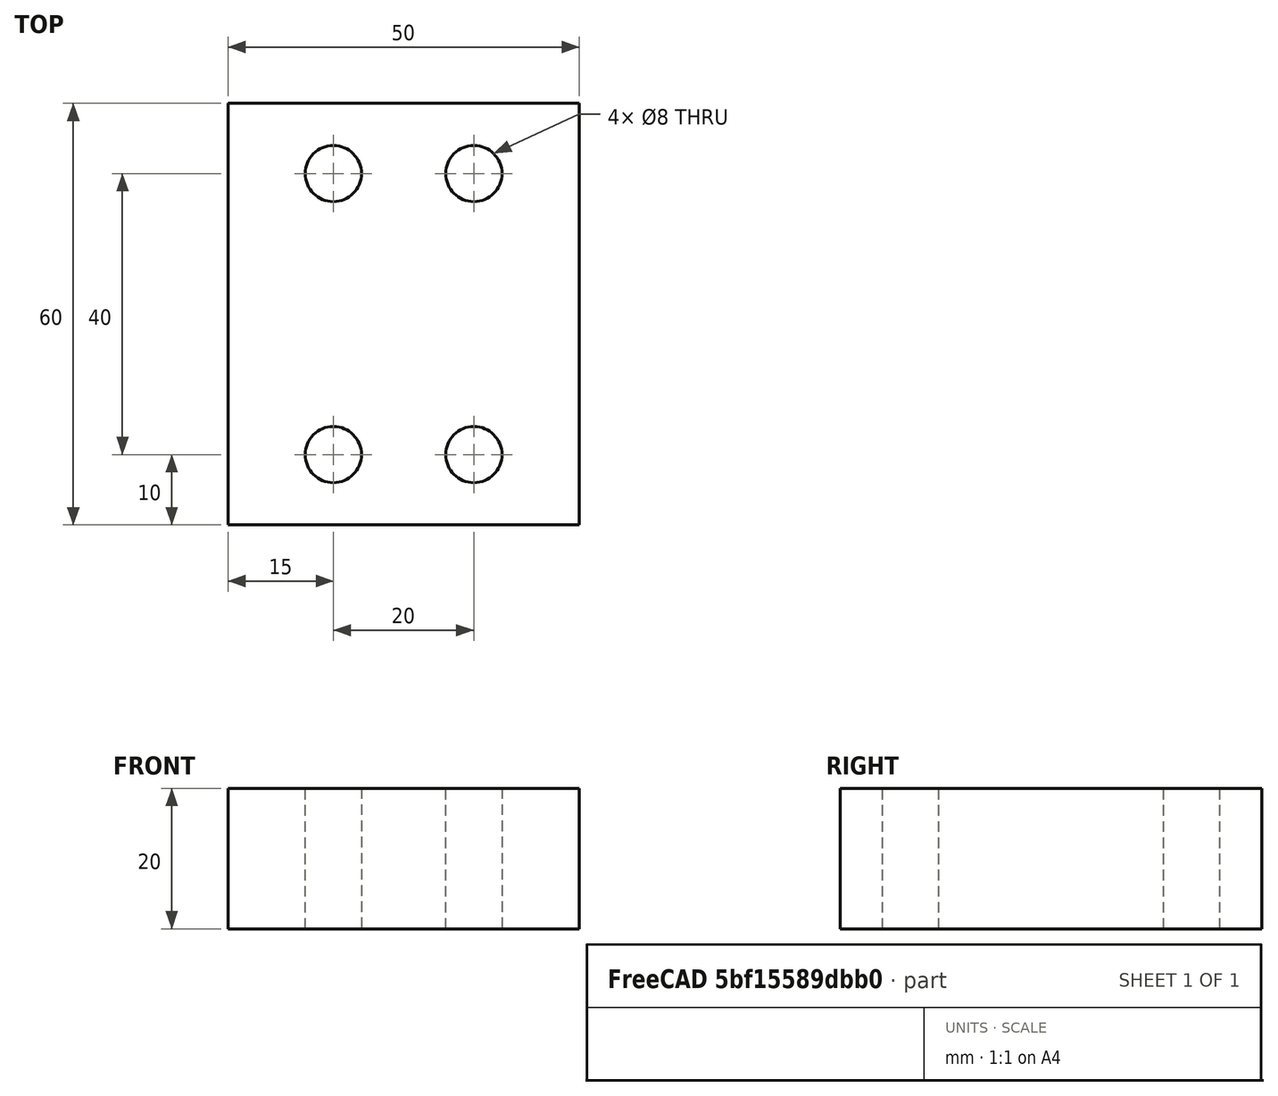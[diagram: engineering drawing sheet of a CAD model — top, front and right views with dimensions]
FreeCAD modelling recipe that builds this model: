
FCSTD DOCUMENT  (FreeCAD 0.19R17089 +1543 (Git))
Label: import-link-001
License: All rights reserved
LicenseURL: http://en.wikipedia.org/wiki/All_rights_reserved
objects: App::FeaturePython×40, Part::FeaturePython×40, App::Link×10, App::LinkElement×8, Sketcher::SketchObject×1, PartDesign::Pad×1, PartDesign::Body×1, App::DocumentObjectGroup×1
note: 40 computed .brp shape members not serialized (recipe doc carries the construction recipe); baked Part::Feature solids carry a one-line shape summary decoded from their .brp
EXTERNAL_REF file=xrepo-lib-003.FCStd obj=Assembly
EXTERNAL_REF file=xrepo-lib-003.FCStd obj=Assembly001
EXTERNAL_REF file=xrepo-lib-003.FCStd obj=Assembly002

FEATURE [Sketcher::SketchObject] Sketch006
  MapMode = 5
  Support = -> [XY_Plane003]
  sketch-geometry (8):
    g0: Circle CenterX=-10 CenterY=20 CenterZ=0 NormalX=0 NormalY=0 NormalZ=1 AngleXU=0 Radius=4
    g1: Circle CenterX=10 CenterY=20 CenterZ=0 NormalX=0 NormalY=0 NormalZ=1 AngleXU=0 Radius=4
    g2: Circle CenterX=10 CenterY=-20 CenterZ=0 NormalX=0 NormalY=0 NormalZ=1 AngleXU=0 Radius=4
    g3: Circle CenterX=-10 CenterY=-20 CenterZ=0 NormalX=0 NormalY=0 NormalZ=1 AngleXU=0 Radius=4
    g4: LineSegment StartX=-25 StartY=30 StartZ=0 EndX=25 EndY=30 EndZ=0
    g5: LineSegment StartX=25 StartY=30 StartZ=0 EndX=25 EndY=-30 EndZ=0
    g6: LineSegment StartX=25 StartY=-30 StartZ=0 EndX=-25 EndY=-30 EndZ=0
    g7: LineSegment StartX=-25 StartY=-30 StartZ=0 EndX=-25 EndY=30 EndZ=0
  constraints (19):
    c: Equal(g0,g1)
    c: Equal(g1,g2)
    c: Equal(g2,g3)
    c: Diameter(g0) = 8  'BHD'
    c: Symmetric(g0,g1,g-2)
    c: Symmetric(g1,g2,g-1)
    c: Symmetric(g0,g3,g-1)
    c: Coincident(g4,g5)
    c: Coincident(g5,g6)
    c: Coincident(g6,g7)
    c: Coincident(g7,g4)
    c: Horizontal(g6)
    c: Vertical(g7)
    c: Symmetric(g4,g4,g-2)
    c: Symmetric(g4,g5,g-1)
    c: Distance(g3,g2) = 20  'L1'
    c: Distance(g4) = 50  'L2'
    c: Distance(g1,g2) = 40  'W1'
    c: Distance(g7) = 60  'W2'
FEATURE [PartDesign::Pad] Pad005
  ClaimChildren = false
  Length = 20
  Length2 = 100
  Profile = -> Sketch006
  Reversed = true
  Type = 0
FEATURE [PartDesign::Body] Body003
  Group = -> [Sketch006,Pad005]
  Origin = -> Origin003
  Tip = -> Pad005
FEATURE [App::FeaturePython] Constraints003  # WARN: FeaturePython — macro-defined, semantics opaque (R4)
  GroupMode = 1
  _Version = 1
FEATURE [Part::FeaturePython] Parts003  # WARN: FeaturePython — macro-defined, semantics opaque (R4)
  Group = -> [Body003]
  GroupMode = 0
FEATURE [App::Link] Link  label="Assembly000 001"
  LinkPlacement = pos=(0,0,-2) rot=(0,0,1;0rad)
  LinkedObject = -> Link007
  Placement = pos=(0,0,-2) rot=(0,0,1;0rad)
FEATURE [App::Link] Link001  label="Assembly001 001"
  LinkedObject = -> Link008
FEATURE [Part::FeaturePython] Parts004  # WARN: FeaturePython — macro-defined, semantics opaque (R4)
  Group = -> [Link,Link001]
  GroupMode = 0
FEATURE [App::Link] Link002  label="Assembly000 002"
  LinkedObject = -> Link007
FEATURE [App::Link] Link003  label="Assembly002 001"
  LinkPlacement = pos=(0,0,2) rot=(0,0,1;0rad)
  LinkedObject = -> Link009
  Placement = pos=(0,0,2) rot=(0,0,1;0rad)
FEATURE [Part::FeaturePython] Parts005  # WARN: FeaturePython — macro-defined, semantics opaque (R4)
  Group = -> [Link002,Link003]
  GroupMode = 0
FEATURE [App::Link] Link004  label="Assembly003 001"
  LinkedObject = -> Assembly003
FEATURE [App::LinkElement] Link005_i0
  LinkPlacement = pos=(-10,20,0) rot=(0,0,1;0rad)
  LinkedObject = -> Assembly005
  Placement = pos=(-10,20,0) rot=(0,0,1;0rad)
FEATURE [App::LinkElement] Link005_i1
  LinkPlacement = pos=(10,20,0) rot=(0,0,1;0rad)
  LinkedObject = -> Assembly005
  Placement = pos=(10,20,0) rot=(0,0,1;0rad)
FEATURE [App::LinkElement] Link005_i2
  LinkPlacement = pos=(10,-20,0) rot=(0,0,1;0rad)
  LinkedObject = -> Assembly005
  Placement = pos=(10,-20,0) rot=(0,0,1;0rad)
FEATURE [App::LinkElement] Link005_i3
  LinkPlacement = pos=(-10,-20,0) rot=(0,0,1;0rad)
  LinkedObject = -> Assembly005
  Placement = pos=(-10,-20,0) rot=(0,0,1;0rad)
FEATURE [App::Link] Link005  label="Assembly005 001"
  ElementCount = 4
  ElementList = -> [Link005_i0,Link005_i1,Link005_i2,Link005_i3]
  LinkedObject = -> Assembly005
FEATURE [App::LinkElement] Link006_i0
  LinkPlacement = pos=(10,20,-33) rot=(0,-1,0;0rad)
  LinkedObject = -> Assembly004
  Placement = pos=(10,20,-33) rot=(0,-1,0;0rad)
FEATURE [App::LinkElement] Link006_i1
  LinkPlacement = pos=(-10,20,-33) rot=(0,-1,0;0rad)
  LinkedObject = -> Assembly004
  Placement = pos=(-10,20,-33) rot=(0,-1,0;0rad)
FEATURE [App::LinkElement] Link006_i2
  LinkPlacement = pos=(-10,-20,-33) rot=(0,-1,0;0rad)
  LinkedObject = -> Assembly004
  Placement = pos=(-10,-20,-33) rot=(0,-1,0;0rad)
FEATURE [App::LinkElement] Link006_i3
  LinkPlacement = pos=(10,-20,-33) rot=(0,-1,0;0rad)
  LinkedObject = -> Assembly004
  Placement = pos=(10,-20,-33) rot=(0,-1,0;0rad)
FEATURE [App::Link] Link006  label="Assembly004 001"
  ElementCount = 4
  ElementList = -> [Link006_i0,Link006_i1,Link006_i2,Link006_i3]
  LinkPlacement = pos=(8.1e-13,6.55651e-06,-55) rot=(0,1,0;3.14159rad)
  LinkedObject = -> Assembly004
  Placement = pos=(8.1e-13,6.55651e-06,-55) rot=(0,1,0;3.14159rad)
FEATURE [Part::FeaturePython] Parts006  # WARN: FeaturePython — macro-defined, semantics opaque (R4)
  Group = -> [Link004,Link005,Link006]
  GroupMode = 0
FEATURE [App::Link] Link007  label="Assembly000 003"
  LinkedObject = -> <external xrepo-lib-003.FCStd>#Assembly
FEATURE [App::Link] Link008  label="Assembly001 002"
  LinkedObject = -> <external xrepo-lib-003.FCStd>#Assembly001
FEATURE [App::Link] Link009  label="Assembly002 002"
  LinkedObject = -> <external xrepo-lib-003.FCStd>#Assembly002
FEATURE [App::DocumentObjectGroup] Group  label="Repository"
  Group = -> [Link007,Link008,Link009,Assembly003,Assembly004,Assembly005]
FEATURE [Part::FeaturePython] Assembly003  label="Assembly003 000"  # WARN: FeaturePython — macro-defined, semantics opaque (R4)
  AutoRelax = true
  BuildShape = 0
  Freeze = false
  Group = -> [Constraints003,Elements003,Parts003]
  GroupMode = 1
  SolverType = 1
  Verbose = false
  _SolverType = 1
  _Version = 1
FEATURE [App::FeaturePython] Elements003  # WARN: FeaturePython — macro-defined, semantics opaque (R4)
  Group = -> [Element005,Element006,Element007,Element008,Element009,Element010,Element011,Element012,Element015]
  GroupMode = 1
FEATURE [Part::FeaturePython] Element005  # link proxy (typed FeaturePython)
  Detach = false
  LinkTransform = true
  LinkedObject = -> Body003 [Pad005.Edge23]
  _Parent = -> Elements003
FEATURE [Part::FeaturePython] Element006  # link proxy (typed FeaturePython)
  Detach = false
  LinkTransform = true
  LinkedObject = -> Body003 [Pad005.Edge20]
  _Parent = -> Elements003
FEATURE [Part::FeaturePython] Element007  # link proxy (typed FeaturePython)
  Detach = false
  LinkTransform = true
  LinkedObject = -> Body003 [Pad005.Edge17]
  _Parent = -> Elements003
FEATURE [Part::FeaturePython] Element008  # link proxy (typed FeaturePython)
  Detach = false
  LinkTransform = true
  LinkedObject = -> Body003 [Pad005.Edge14]
  _Parent = -> Elements003
FEATURE [Part::FeaturePython] Element009  # link proxy (typed FeaturePython)
  Detach = false
  LinkTransform = true
  LinkedObject = -> Body003 [Pad005.Edge24]
  _Parent = -> Elements003
FEATURE [Part::FeaturePython] Element010  # link proxy (typed FeaturePython)
  Detach = false
  LinkTransform = true
  LinkedObject = -> Body003 [Pad005.Edge21]
  _Parent = -> Elements003
FEATURE [Part::FeaturePython] Element011  # link proxy (typed FeaturePython)
  Detach = false
  LinkTransform = true
  LinkedObject = -> Body003 [Pad005.Edge18]
  _Parent = -> Elements003
FEATURE [Part::FeaturePython] Element012  # link proxy (typed FeaturePython)
  Detach = false
  LinkTransform = true
  LinkedObject = -> Body003 [Pad005.Edge15]
  _Parent = -> Elements003
FEATURE [Part::FeaturePython] Assembly004  label="Assembly004 000"  # WARN: FeaturePython — macro-defined, semantics opaque (R4)
  AutoRelax = true
  BuildShape = 0
  Freeze = false
  Group = -> [Constraints004,Elements004,Parts004]
  GroupMode = 1
  SolverType = 1
  Verbose = false
  _SolverType = 1
  _Version = 1
FEATURE [App::FeaturePython] Constraints004  # WARN: FeaturePython — macro-defined, semantics opaque (R4)
  Group = -> [Constraint]
  GroupMode = 1
  _Version = 1
FEATURE [App::FeaturePython] Elements004  # WARN: FeaturePython — macro-defined, semantics opaque (R4)
  Group = -> [_Element,_Element001,Element013]
  GroupMode = 1
FEATURE [App::FeaturePython] Constraint  label="PlaneCoincident"  # WARN: FeaturePython — macro-defined, semantics opaque (R4)
  Angle = 0
  AnglePitch = 0
  AngleRoll = 0
  Cascade = false
  ConstraintType = 2
  Disabled = false
  Group = -> [ElementLink,ElementLink001]
  GroupMode = 1
  LockAngle = false
  Multiply = false
  OffsetX = 0
  OffsetY = 0
  _ConstraintType = 35
  _Parent = -> Constraints004
FEATURE [App::FeaturePython] ElementLink  label="_Element"  # link proxy (typed FeaturePython)
  LinkTransform = true
  LinkedObject = -> _Element
  _Parent = -> Constraint
FEATURE [Part::FeaturePython] _Element  # link proxy (typed FeaturePython)
  Detach = false
  LinkTransform = true
  LinkedObject = -> Link001 [1.$Element002.]
  _Parent = -> Elements004
FEATURE [App::FeaturePython] ElementLink001  label="_Element001"  # link proxy (typed FeaturePython)
  LinkTransform = true
  LinkedObject = -> _Element001
  _Parent = -> Constraint
FEATURE [Part::FeaturePython] _Element001  # link proxy (typed FeaturePython)
  Detach = false
  LinkTransform = true
  LinkedObject = -> Link [1.$Element001.]
  _Parent = -> Elements004
FEATURE [Part::FeaturePython] Element013  # link proxy (typed FeaturePython)
  Detach = false
  LinkTransform = true
  LinkedObject = -> Link [1.$Element.]
  _Parent = -> Elements004
FEATURE [Part::FeaturePython] Assembly005  label="Assembly005 000"  # WARN: FeaturePython — macro-defined, semantics opaque (R4)
  AutoRelax = true
  BuildShape = 0
  Freeze = false
  Group = -> [Constraints005,Elements005,Parts005]
  GroupMode = 1
  SolverType = 1
  Verbose = false
  _SolverType = 1
  _Version = 1
FEATURE [App::FeaturePython] Constraints005  # WARN: FeaturePython — macro-defined, semantics opaque (R4)
  Group = -> [Constraint001]
  GroupMode = 1
  _Version = 1
FEATURE [App::FeaturePython] Elements005  # WARN: FeaturePython — macro-defined, semantics opaque (R4)
  Group = -> [_Element002,_Element003,Element014]
  GroupMode = 1
FEATURE [App::FeaturePython] Constraint001  label="PlaneCoincident001"  # WARN: FeaturePython — macro-defined, semantics opaque (R4)
  Angle = 0
  AnglePitch = 0
  AngleRoll = 0
  Cascade = false
  ConstraintType = 2
  Disabled = false
  Group = -> [ElementLink002,ElementLink003]
  GroupMode = 1
  LockAngle = false
  Multiply = false
  OffsetX = 0
  OffsetY = 0
  _ConstraintType = 35
  _Parent = -> Constraints005
FEATURE [App::FeaturePython] ElementLink002  label="_Element002"  # link proxy (typed FeaturePython)
  LinkTransform = true
  LinkedObject = -> _Element002
  _Parent = -> Constraint001
FEATURE [Part::FeaturePython] _Element002  # link proxy (typed FeaturePython)
  Detach = false
  LinkTransform = true
  LinkedObject = -> Link002 [1.$Element001.]
  _Parent = -> Elements005
FEATURE [App::FeaturePython] ElementLink003  label="_Element003"  # link proxy (typed FeaturePython)
  LinkTransform = true
  LinkedObject = -> _Element003
  _Parent = -> Constraint001
FEATURE [Part::FeaturePython] _Element003  # link proxy (typed FeaturePython)
  Detach = false
  LinkTransform = true
  LinkedObject = -> Link003 [1.$Element004.]
  _Parent = -> Elements005
FEATURE [Part::FeaturePython] Element014  # link proxy (typed FeaturePython)
  Detach = false
  LinkTransform = true
  LinkedObject = -> Link002 [1.$Element.]
  _Parent = -> Elements005
FEATURE [Part::FeaturePython] Assembly006  label="Assembly006 000"  # WARN: FeaturePython — macro-defined, semantics opaque (R4)
  AutoRelax = true
  BuildShape = 0
  Freeze = false
  Group = -> [Constraints006,Elements006,Parts006]
  GroupMode = 1
  SolverType = 1
  Verbose = false
  _SolverType = 1
  _Version = 1
FEATURE [App::FeaturePython] Constraints006  # WARN: FeaturePython — macro-defined, semantics opaque (R4)
  Group = -> [Constraint002,Constraint003,Constraint004,Constraint005,Constraint006,Constraint007,Constraint008,Constraint009,Constraint010]
  GroupMode = 1
  _Version = 1
FEATURE [App::FeaturePython] Elements006  # WARN: FeaturePython — macro-defined, semantics opaque (R4)
  Group = -> [_Element004,_Element005,_Element006,_Element007,_Element008,_Element009,_Element010,_Element011,_Element012,_Element013,_Element014,_Element015,_Element016,_Element017,_Element018,_Element019,_Element020]
  GroupMode = 1
FEATURE [App::FeaturePython] Constraint002  label="Locked"  # WARN: FeaturePython — macro-defined, semantics opaque (R4)
  ConstraintType = 0
  Disabled = false
  Group = -> [ElementLink004]
  GroupMode = 1
  _ConstraintType = 0
  _Parent = -> Constraints006
FEATURE [App::FeaturePython] ElementLink004  label="_Element004"  # link proxy (typed FeaturePython)
  LinkTransform = true
  LinkedObject = -> _Element004
  _Parent = -> Constraint002
FEATURE [Part::FeaturePython] Element015  # link proxy (typed FeaturePython)
  Detach = false
  LinkTransform = true
  LinkedObject = -> Body003 [Pad005.Face9]
  _Parent = -> Elements003
FEATURE [Part::FeaturePython] _Element004  # link proxy (typed FeaturePython)
  Detach = false
  LinkTransform = true
  LinkedObject = -> Link004 [1.$Element015.]
  _Parent = -> Elements006
FEATURE [App::FeaturePython] Constraint003  label="PlaneCoincident002"  # WARN: FeaturePython — macro-defined, semantics opaque (R4)
  Angle = 0
  AnglePitch = 0
  AngleRoll = 0
  Cascade = false
  ConstraintType = 2
  Disabled = false
  Group = -> [ElementLink005,ElementLink006]
  GroupMode = 1
  LockAngle = false
  Multiply = false
  OffsetX = 0
  OffsetY = 0
  _ConstraintType = 35
  _Parent = -> Constraints006
FEATURE [App::FeaturePython] ElementLink005  label="_Element005"  # link proxy (typed FeaturePython)
  LinkTransform = true
  LinkedObject = -> _Element005
  _Parent = -> Constraint003
FEATURE [Part::FeaturePython] _Element005  # link proxy (typed FeaturePython)
  Detach = false
  LinkTransform = true
  LinkedObject = -> Link005 [Link005_i0.1.$Element014.]
  _Parent = -> Elements006
FEATURE [App::FeaturePython] ElementLink006  label="_Element006"  # link proxy (typed FeaturePython)
  LinkTransform = true
  LinkedObject = -> _Element006
  _Parent = -> Constraint003
FEATURE [Part::FeaturePython] _Element006  # link proxy (typed FeaturePython)
  Detach = false
  LinkTransform = true
  LinkedObject = -> Link004 [1.$Element005.]
  _Parent = -> Elements006
FEATURE [App::FeaturePython] Constraint004  label="PlaneCoincident003"  # WARN: FeaturePython — macro-defined, semantics opaque (R4)
  Angle = 0
  AnglePitch = 0
  AngleRoll = 0
  Cascade = false
  ConstraintType = 2
  Disabled = false
  Group = -> [ElementLink007,ElementLink008]
  GroupMode = 1
  LockAngle = false
  Multiply = false
  OffsetX = 0
  OffsetY = 0
  _ConstraintType = 35
  _Parent = -> Constraints006
FEATURE [App::FeaturePython] ElementLink007  label="_Element007"  # link proxy (typed FeaturePython)
  LinkTransform = true
  LinkedObject = -> _Element007
  _Parent = -> Constraint004
FEATURE [Part::FeaturePython] _Element007  # link proxy (typed FeaturePython)
  Detach = false
  LinkTransform = true
  LinkedObject = -> Link004 [1.$Element006.]
  _Parent = -> Elements006
FEATURE [App::FeaturePython] ElementLink008  label="_Element008"  # link proxy (typed FeaturePython)
  LinkTransform = true
  LinkedObject = -> _Element008
  _Parent = -> Constraint004
FEATURE [Part::FeaturePython] _Element008  # link proxy (typed FeaturePython)
  Detach = false
  LinkTransform = true
  LinkedObject = -> Link005 [Link005_i1.1.$Element014.]
  _Parent = -> Elements006
FEATURE [App::FeaturePython] Constraint005  label="PlaneCoincident004"  # WARN: FeaturePython — macro-defined, semantics opaque (R4)
  Angle = 0
  AnglePitch = 0
  AngleRoll = 0
  Cascade = false
  ConstraintType = 2
  Disabled = false
  Group = -> [ElementLink009,ElementLink010]
  GroupMode = 1
  LockAngle = false
  Multiply = false
  OffsetX = 0
  OffsetY = 0
  _ConstraintType = 35
  _Parent = -> Constraints006
FEATURE [App::FeaturePython] ElementLink009  label="_Element009"  # link proxy (typed FeaturePython)
  LinkTransform = true
  LinkedObject = -> _Element009
  _Parent = -> Constraint005
FEATURE [Part::FeaturePython] _Element009  # link proxy (typed FeaturePython)
  Detach = false
  LinkTransform = true
  LinkedObject = -> Link004 [1.$Element007.]
  _Parent = -> Elements006
FEATURE [App::FeaturePython] ElementLink010  label="_Element010"  # link proxy (typed FeaturePython)
  LinkTransform = true
  LinkedObject = -> _Element010
  _Parent = -> Constraint005
FEATURE [Part::FeaturePython] _Element010  # link proxy (typed FeaturePython)
  Detach = false
  LinkTransform = true
  LinkedObject = -> Link005 [Link005_i2.1.$Element014.]
  _Parent = -> Elements006
FEATURE [App::FeaturePython] Constraint006  label="PlaneCoincident005"  # WARN: FeaturePython — macro-defined, semantics opaque (R4)
  Angle = 0
  AnglePitch = 0
  AngleRoll = 0
  Cascade = false
  ConstraintType = 2
  Disabled = false
  Group = -> [ElementLink011,ElementLink012]
  GroupMode = 1
  LockAngle = false
  Multiply = false
  OffsetX = 0
  OffsetY = 0
  _ConstraintType = 35
  _Parent = -> Constraints006
FEATURE [App::FeaturePython] ElementLink011  label="_Element011"  # link proxy (typed FeaturePython)
  LinkTransform = true
  LinkedObject = -> _Element011
  _Parent = -> Constraint006
FEATURE [Part::FeaturePython] _Element011  # link proxy (typed FeaturePython)
  Detach = false
  LinkTransform = true
  LinkedObject = -> Link004 [1.$Element008.]
  _Parent = -> Elements006
FEATURE [App::FeaturePython] ElementLink012  label="_Element012"  # link proxy (typed FeaturePython)
  LinkTransform = true
  LinkedObject = -> _Element012
  _Parent = -> Constraint006
FEATURE [Part::FeaturePython] _Element012  # link proxy (typed FeaturePython)
  Detach = false
  LinkTransform = true
  LinkedObject = -> Link005 [Link005_i3.1.$Element014.]
  _Parent = -> Elements006
FEATURE [App::FeaturePython] Constraint007  label="PlaneCoincident006"  # WARN: FeaturePython — macro-defined, semantics opaque (R4)
  Angle = 0
  AnglePitch = 0
  AngleRoll = 0
  Cascade = false
  ConstraintType = 2
  Disabled = false
  Group = -> [ElementLink013,ElementLink014]
  GroupMode = 1
  LockAngle = false
  Multiply = false
  OffsetX = 0
  OffsetY = 0
  _ConstraintType = 35
  _Parent = -> Constraints006
FEATURE [App::FeaturePython] ElementLink013  label="_Element013"  # link proxy (typed FeaturePython)
  LinkTransform = true
  LinkedObject = -> _Element013
  _Parent = -> Constraint007
FEATURE [Part::FeaturePython] _Element013  # link proxy (typed FeaturePython)
  Detach = false
  LinkTransform = true
  LinkedObject = -> Link004 [1.$Element009.]
  _Parent = -> Elements006
FEATURE [App::FeaturePython] ElementLink014  label="_Element014"  # link proxy (typed FeaturePython)
  LinkTransform = true
  LinkedObject = -> _Element014
  _Parent = -> Constraint007
FEATURE [Part::FeaturePython] _Element014  # link proxy (typed FeaturePython)
  Detach = false
  LinkTransform = true
  LinkedObject = -> Link006 [Link006_i0.1.$Element013.]
  _Parent = -> Elements006
FEATURE [App::FeaturePython] Constraint008  label="PlaneCoincident007"  # WARN: FeaturePython — macro-defined, semantics opaque (R4)
  Angle = 0
  AnglePitch = 0
  AngleRoll = 0
  Cascade = false
  ConstraintType = 2
  Disabled = false
  Group = -> [ElementLink015,ElementLink016]
  GroupMode = 1
  LockAngle = false
  Multiply = false
  OffsetX = 0
  OffsetY = 0
  _ConstraintType = 35
  _Parent = -> Constraints006
FEATURE [App::FeaturePython] ElementLink015  label="_Element015"  # link proxy (typed FeaturePython)
  LinkTransform = true
  LinkedObject = -> _Element015
  _Parent = -> Constraint008
FEATURE [Part::FeaturePython] _Element015  # link proxy (typed FeaturePython)
  Detach = false
  LinkTransform = true
  LinkedObject = -> Link004 [1.$Element010.]
  _Parent = -> Elements006
FEATURE [App::FeaturePython] ElementLink016  label="_Element016"  # link proxy (typed FeaturePython)
  LinkTransform = true
  LinkedObject = -> _Element016
  _Parent = -> Constraint008
FEATURE [Part::FeaturePython] _Element016  # link proxy (typed FeaturePython)
  Detach = false
  LinkTransform = true
  LinkedObject = -> Link006 [Link006_i1.1.$Element013.]
  _Parent = -> Elements006
FEATURE [App::FeaturePython] Constraint009  label="PlaneCoincident008"  # WARN: FeaturePython — macro-defined, semantics opaque (R4)
  Angle = 0
  AnglePitch = 0
  AngleRoll = 0
  Cascade = false
  ConstraintType = 2
  Disabled = false
  Group = -> [ElementLink017,ElementLink018]
  GroupMode = 1
  LockAngle = false
  Multiply = false
  OffsetX = 0
  OffsetY = 0
  _ConstraintType = 35
  _Parent = -> Constraints006
FEATURE [App::FeaturePython] ElementLink017  label="_Element017"  # link proxy (typed FeaturePython)
  LinkTransform = true
  LinkedObject = -> _Element017
  _Parent = -> Constraint009
FEATURE [Part::FeaturePython] _Element017  # link proxy (typed FeaturePython)
  Detach = false
  LinkTransform = true
  LinkedObject = -> Link004 [1.$Element011.]
  _Parent = -> Elements006
FEATURE [App::FeaturePython] ElementLink018  label="_Element018"  # link proxy (typed FeaturePython)
  LinkTransform = true
  LinkedObject = -> _Element018
  _Parent = -> Constraint009
FEATURE [Part::FeaturePython] _Element018  # link proxy (typed FeaturePython)
  Detach = false
  LinkTransform = true
  LinkedObject = -> Link006 [Link006_i2.1.$Element013.]
  _Parent = -> Elements006
FEATURE [App::FeaturePython] Constraint010  label="PlaneCoincident009"  # WARN: FeaturePython — macro-defined, semantics opaque (R4)
  Angle = 0
  AnglePitch = 0
  AngleRoll = 0
  Cascade = false
  ConstraintType = 2
  Disabled = false
  Group = -> [ElementLink019,ElementLink020]
  GroupMode = 1
  LockAngle = false
  Multiply = false
  OffsetX = 0
  OffsetY = 0
  _ConstraintType = 35
  _Parent = -> Constraints006
FEATURE [App::FeaturePython] ElementLink019  label="_Element019"  # link proxy (typed FeaturePython)
  LinkTransform = true
  LinkedObject = -> _Element019
  _Parent = -> Constraint010
FEATURE [Part::FeaturePython] _Element019  # link proxy (typed FeaturePython)
  Detach = false
  LinkTransform = true
  LinkedObject = -> Link004 [1.$Element012.]
  _Parent = -> Elements006
FEATURE [App::FeaturePython] ElementLink020  label="_Element020"  # link proxy (typed FeaturePython)
  LinkTransform = true
  LinkedObject = -> _Element020
  _Parent = -> Constraint010
FEATURE [Part::FeaturePython] _Element020  # link proxy (typed FeaturePython)
  Detach = false
  LinkTransform = true
  LinkedObject = -> Link006 [Link006_i3.1.$Element013.]
  _Parent = -> Elements006

RESOLVED EXTERNAL PARTS (link-assembly join: the EXTERNAL_REF files above that resolve inside this repo's crawl, each included once):
---- part xrepo-lib-003.FCStd = doc fcstd_cd6cd5374638 ----
FCSTD DOCUMENT  (FreeCAD 0.19R17089 +1543 (Git))
Label: xrepo-lib-003
License: All rights reserved
LicenseURL: http://en.wikipedia.org/wiki/All_rights_reserved
objects: Part::FeaturePython×14, Sketcher::SketchObject×9, App::FeaturePython×8, PartDesign::Pad×8, PartDesign::Body×4, PartDesign::Chamfer×2, PartDesign::Pocket×1
note: 43 computed .brp shape members not serialized (recipe doc carries the construction recipe); baked Part::Feature solids carry a one-line shape summary decoded from their .brp

FEATURE [App::FeaturePython] Constraints  # WARN: FeaturePython — macro-defined, semantics opaque (R4)
  GroupMode = 1
  _Version = 1
FEATURE [Sketcher::SketchObject] Sketch
  MapMode = 5
  Support = -> [XY_Plane]
  sketch-geometry (2):
    g0: Circle CenterX=0 CenterY=0 CenterZ=0 NormalX=0 NormalY=0 NormalZ=1 AngleXU=0 Radius=4.15
    g1: Circle CenterX=0 CenterY=0 CenterZ=0 NormalX=0 NormalY=0 NormalZ=1 AngleXU=0 Radius=8
  constraints (4):
    c: Coincident(g0,g-1)
    c: Coincident(g1,g0)
    c: Diameter(g0) = 8.3  'D1'
    c: Diameter(g1) = 16  'D2'
FEATURE [PartDesign::Pad] Pad
  ClaimChildren = false
  Length = 2
  Length2 = 100
  Profile = -> Sketch
  Type = 0
FEATURE [PartDesign::Body] Body
  Group = -> [Sketch,Pad]
  Origin = -> Origin
  Tip = -> Pad
FEATURE [Part::FeaturePython] Parts  # WARN: FeaturePython — macro-defined, semantics opaque (R4)
  Group = -> [Body]
  GroupMode = 0
FEATURE [App::FeaturePython] Constraints001  # WARN: FeaturePython — macro-defined, semantics opaque (R4)
  GroupMode = 1
  _Version = 1
FEATURE [Sketcher::SketchObject] Sketch001
  MapMode = 5
  Support = -> [XY_Plane001]
  sketch-geometry (8):
    g0: Circle CenterX=0 CenterY=0 CenterZ=0 NormalX=0 NormalY=0 NormalZ=1 AngleXU=0 Radius=4
    g1: LineSegment StartX=7.50496 StartY=0.0945881 StartZ=0 EndX=3.67056 EndY=6.54678 EndZ=0
    g2: LineSegment StartX=3.67056 StartY=6.54678 StartZ=0 EndX=-3.83439 EndY=6.45219 EndZ=0
    g3: LineSegment StartX=-3.83439 StartY=6.45219 StartZ=0 EndX=-7.50496 EndY=-0.0945881 EndZ=0
    g4: LineSegment StartX=-7.50496 StartY=-0.0945881 StartZ=0 EndX=-3.67056 EndY=-6.54678 EndZ=0
    g5: LineSegment StartX=-3.67056 StartY=-6.54678 StartZ=0 EndX=3.83439 EndY=-6.45219 EndZ=0
    g6: LineSegment StartX=3.83439 StartY=-6.45219 StartZ=0 EndX=7.50496 EndY=0.0945881 EndZ=0
    g7: Circle [constr] CenterX=0 CenterY=0 CenterZ=0 NormalX=0 NormalY=0 NormalZ=1 AngleXU=0 Radius=7.50555
  constraints (17):
    c: Coincident(g0,g-1)
    c: Diameter(g0) = 8  'D1'
    c: Coincident(g1,g2)
    c: Coincident(g2,g3)
    c: Coincident(g3,g4)
    c: Coincident(g4,g5)
    c: Coincident(g5,g6)
    c: Coincident(g6,g1)
    c: Equal(g1, g2-g6) x5
    c: PointOnObject(g1,g7)
    c: PointOnObject(g2,g7)
    c: PointOnObject(g3,g7)
    c: PointOnObject(g4,g7)
    c: PointOnObject(g5,g7)
    c: PointOnObject(g6,g7)
    c: Coincident(g7,g0)
    c: Distance(g1,g5) = 13  'WS'
FEATURE [PartDesign::Pad] Pad001
  ClaimChildren = false
  Length = 6.4
  Length2 = 100
  Profile = -> Sketch001
  Type = 0
FEATURE [PartDesign::Body] Body001
  Group = -> [Sketch001,Pad001]
  Origin = -> Origin001
  Tip = -> Pad001
FEATURE [Part::FeaturePython] Parts001  # WARN: FeaturePython — macro-defined, semantics opaque (R4)
  Group = -> [Body001]
  GroupMode = 0
FEATURE [App::FeaturePython] Constraints002  # WARN: FeaturePython — macro-defined, semantics opaque (R4)
  GroupMode = 1
  _Version = 1
FEATURE [Sketcher::SketchObject] Sketch004
  MapMode = 5
  Support = -> [XY_Plane002]
  sketch-geometry (1):
    g0: Circle CenterX=0 CenterY=0 CenterZ=0 NormalX=0 NormalY=0 NormalZ=1 AngleXU=0 Radius=6.5
  constraints (2):
    c: Coincident(g0,g-1)
    c: Diameter(g0) = 13  'DH'
FEATURE [Sketcher::SketchObject] Sketch002
  MapMode = 5
  Support = -> [XY_Plane002]
  sketch-geometry (1):
    g0: Circle CenterX=0 CenterY=0 CenterZ=0 NormalX=0 NormalY=0 NormalZ=1 AngleXU=0 Radius=4
  constraints (2):
    c: Coincident(g0,g-1)
    c: Diameter(g0) = 8  'D1'
FEATURE [PartDesign::Pad] Pad002
  ClaimChildren = false
  Length = 5
  Length2 = 100
  Profile = -> Sketch002
  Reversed = true
  Type = 0
FEATURE [Sketcher::SketchObject] Sketch003
  ExternalGeometry = -> [Pad002]
  MapMode = 5
  Placement = pos=(0,0,-5) rot=(1,0,0;3.14159rad)
  Support = -> [Pad002]
FEATURE [PartDesign::Pad] Pad003
  BaseFeature = -> Pad002
  ClaimChildren = false
  Length = 30
  Length2 = 100
  Profile = -> Sketch003
  Type = 0
FEATURE [PartDesign::Pad] Pad004
  BaseFeature = -> Pad003
  ClaimChildren = false
  Length = 6
  Length2 = 100
  Profile = -> Sketch004
  Type = 0
FEATURE [Sketcher::SketchObject] Sketch005
  MapMode = 5
  Placement = pos=(0,0,6) rot=(0,0,1;0rad)
  Support = -> [Pad004]
  sketch-geometry (7):
    g0: LineSegment StartX=3.4641 StartY=0 StartZ=0 EndX=1.73205 EndY=3 EndZ=0
    g1: LineSegment StartX=1.73205 StartY=3 StartZ=0 EndX=-1.73205 EndY=3 EndZ=0
    g2: LineSegment StartX=-1.73205 StartY=3 StartZ=0 EndX=-3.4641 EndY=0 EndZ=0
    g3: LineSegment StartX=-3.4641 StartY=0 StartZ=0 EndX=-1.73205 EndY=-3 EndZ=0
    g4: LineSegment StartX=-1.73205 StartY=-3 StartZ=0 EndX=1.73205 EndY=-3 EndZ=0
    g5: LineSegment StartX=1.73205 StartY=-3 StartZ=0 EndX=3.4641 EndY=0 EndZ=0
    g6: Circle [constr] CenterX=0 CenterY=0 CenterZ=0 NormalX=0 NormalY=0 NormalZ=1 AngleXU=0 Radius=3.4641
  constraints (16):
    c: Coincident(g0,g1)
    c: Coincident(g1,g2)
    c: Coincident(g2,g3)
    c: Coincident(g3,g4)
    c: Coincident(g4,g5)
    c: Coincident(g5,g0)
    c: Equal(g0, g1-g5) x5
    c: PointOnObject(g0,g6)
    c: PointOnObject(g1,g6)
    c: PointOnObject(g2,g6)
    c: PointOnObject(g3,g6)
    c: PointOnObject(g4,g6)
    c: PointOnObject(g5,g6)
    c: Coincident(g6,g-1)
    c: PointOnObject(g5,g-1)
    c: Distance(g0,g4) = 6  'WS'
FEATURE [PartDesign::Pocket] Pocket
  BaseFeature = -> Pad004
  ClaimChildren = false
  Length = 5
  Length2 = 100
  Profile = -> Sketch005
  Type = 0
FEATURE [PartDesign::Chamfer] Chamfer
  Base = -> Pocket [Edge6]
  BaseFeature = -> Pocket
  Size = 1.2
FEATURE [PartDesign::Body] Body002
  Group = -> [Sketch002,Pad002,Sketch003,Pad003,Sketch004,Pad004,Sketch005,Pocket,Chamfer]
  Origin = -> Origin002
  Tip = -> Chamfer
FEATURE [Part::FeaturePython] Parts002  # WARN: FeaturePython — macro-defined, semantics opaque (R4)
  Group = -> [Body002]
  GroupMode = 0
FEATURE [App::FeaturePython] Constraints003  # WARN: FeaturePython — macro-defined, semantics opaque (R4)
  GroupMode = 1
  _Version = 1
FEATURE [Sketcher::SketchObject] Sketch006
  MapMode = 5
  Support = -> [XY_Plane003]
  sketch-geometry (1):
    g0: Circle CenterX=0 CenterY=0 CenterZ=0 NormalX=0 NormalY=0 NormalZ=1 AngleXU=0 Radius=4
  constraints (2):
    c: Coincident(g0,g-1)
    c: Diameter(g0) = 8  'D1'
FEATURE [PartDesign::Pad] Pad005
  ClaimChildren = false
  Length = 5
  Length2 = 100
  Profile = -> Sketch006
  Reversed = true
  Type = 0
FEATURE [Sketcher::SketchObject] Sketch007
  ExternalGeometry = -> [Pad005]
  MapMode = 5
  Placement = pos=(0,0,-5) rot=(1,0,0;3.14159rad)
  Support = -> [Pad005]
FEATURE [PartDesign::Pad] Pad006
  BaseFeature = -> Pad005
  ClaimChildren = false
  Length = 30
  Length2 = 100
  Profile = -> Sketch007
  Type = 0
FEATURE [PartDesign::Chamfer] Chamfer001
  Base = -> Pad006 [Edge5]
  BaseFeature = -> Pad006
  Size = 1.2
FEATURE [Sketcher::SketchObject] Sketch008
  MapMode = 5
  Support = -> [XY_Plane003]
  sketch-geometry (7):
    g0: LineSegment StartX=7.50555 StartY=0 StartZ=0 EndX=3.75278 EndY=6.5 EndZ=0
    g1: LineSegment StartX=3.75278 StartY=6.5 StartZ=0 EndX=-3.75278 EndY=6.5 EndZ=0
    g2: LineSegment StartX=-3.75278 StartY=6.5 StartZ=0 EndX=-7.50555 EndY=3.3924e-11 EndZ=0
    g3: LineSegment StartX=-7.50555 StartY=3.3924e-11 StartZ=0 EndX=-3.75278 EndY=-6.5 EndZ=0
    g4: LineSegment StartX=-3.75278 StartY=-6.5 StartZ=0 EndX=3.75278 EndY=-6.5 EndZ=0
    g5: LineSegment StartX=3.75278 StartY=-6.5 StartZ=0 EndX=7.50555 EndY=0 EndZ=0
    g6: Circle [constr] CenterX=0 CenterY=0 CenterZ=0 NormalX=0 NormalY=0 NormalZ=1 AngleXU=0 Radius=7.50555
  constraints (16):
    c: Coincident(g0,g1)
    c: Coincident(g1,g2)
    c: Coincident(g2,g3)
    c: Coincident(g3,g4)
    c: Coincident(g4,g5)
    c: Coincident(g5,g0)
    c: Equal(g0, g1-g5) x5
    c: PointOnObject(g0,g6)
    c: PointOnObject(g1,g6)
    c: PointOnObject(g2,g6)
    c: PointOnObject(g3,g6)
    c: PointOnObject(g4,g6)
    c: PointOnObject(g5,g6)
    c: Coincident(g6,g-1)
    c: PointOnObject(g5,g-1)
    c: Distance(g0,g4) = 13  'WS'
FEATURE [PartDesign::Pad] Pad007
  BaseFeature = -> Chamfer001
  ClaimChildren = false
  Length = 6.4
  Length2 = 100
  Profile = -> Sketch008
  Type = 0
FEATURE [PartDesign::Body] Body003
  Group = -> [Sketch006,Pad005,Sketch007,Pad006,Chamfer001,Sketch008,Pad007]
  Origin = -> Origin003
  Tip = -> Pad007
FEATURE [Part::FeaturePython] Parts003  # WARN: FeaturePython — macro-defined, semantics opaque (R4)
  Group = -> [Body003]
  GroupMode = 0
FEATURE [Part::FeaturePython] Element  # link proxy (typed FeaturePython)
  Detach = false
  LinkTransform = true
  LinkedObject = -> Body [Pad.Edge5]
  _Parent = -> Elements
FEATURE [Part::FeaturePython] Element001  # link proxy (typed FeaturePython)
  Detach = false
  LinkTransform = true
  LinkedObject = -> Body [Pad.Edge6]
  _Parent = -> Elements
FEATURE [App::FeaturePython] Elements  # WARN: FeaturePython — macro-defined, semantics opaque (R4)
  Group = -> [Element,Element001]
  GroupMode = 1
FEATURE [Part::FeaturePython] Assembly  label="Assembly000 000"  # WARN: FeaturePython — macro-defined, semantics opaque (R4)
  AutoRelax = true
  BuildShape = 0
  Freeze = false
  Group = -> [Constraints,Elements,Parts]
  GroupMode = 1
  SolverType = 1
  Verbose = false
  _SolverType = 1
  _Version = 1
FEATURE [Part::FeaturePython] Element002  # link proxy (typed FeaturePython)
  Detach = false
  LinkTransform = true
  LinkedObject = -> Body001 [Pad001.Edge20]
  _Parent = -> Elements001
FEATURE [Part::FeaturePython] Element003  # link proxy (typed FeaturePython)
  Detach = false
  LinkTransform = true
  LinkedObject = -> Body001 [Pad001.Edge21]
  _Parent = -> Elements001
FEATURE [App::FeaturePython] Elements001  # WARN: FeaturePython — macro-defined, semantics opaque (R4)
  Group = -> [Element002,Element003]
  GroupMode = 1
FEATURE [Part::FeaturePython] Assembly001  label="Assembly001 000"  # WARN: FeaturePython — macro-defined, semantics opaque (R4)
  AutoRelax = true
  BuildShape = 0
  Freeze = false
  Group = -> [Constraints001,Elements001,Parts001]
  GroupMode = 1
  SolverType = 1
  Verbose = false
  _SolverType = 1
  _Version = 1
FEATURE [Part::FeaturePython] Element004  # link proxy (typed FeaturePython)
  Detach = false
  LinkTransform = true
  LinkedObject = -> Body002 [Pad002.Edge2]
  _Parent = -> Elements002
FEATURE [App::FeaturePython] Elements002  # WARN: FeaturePython — macro-defined, semantics opaque (R4)
  Group = -> [Element004]
  GroupMode = 1
FEATURE [Part::FeaturePython] Assembly002  label="Assembly002 000"  # WARN: FeaturePython — macro-defined, semantics opaque (R4)
  AutoRelax = true
  BuildShape = 0
  Freeze = false
  Group = -> [Constraints002,Elements002,Parts002]
  GroupMode = 1
  SolverType = 1
  Verbose = false
  _SolverType = 1
  _Version = 1
FEATURE [Part::FeaturePython] Assembly003  label="Assembly003 000"  # WARN: FeaturePython — macro-defined, semantics opaque (R4)
  AutoRelax = true
  BuildShape = 0
  Freeze = false
  Group = -> [Constraints003,Elements003,Parts003]
  GroupMode = 1
  SolverType = 1
  Verbose = false
  _SolverType = 1
  _Version = 1
FEATURE [App::FeaturePython] Elements003  # WARN: FeaturePython — macro-defined, semantics opaque (R4)
  Group = -> [Element005]
  GroupMode = 1
FEATURE [Part::FeaturePython] Element005  label="Element004"  # link proxy (typed FeaturePython)
  Detach = false
  LinkTransform = true
  LinkedObject = -> Body003 [Pad007.Edge7]
  _Parent = -> Elements003
